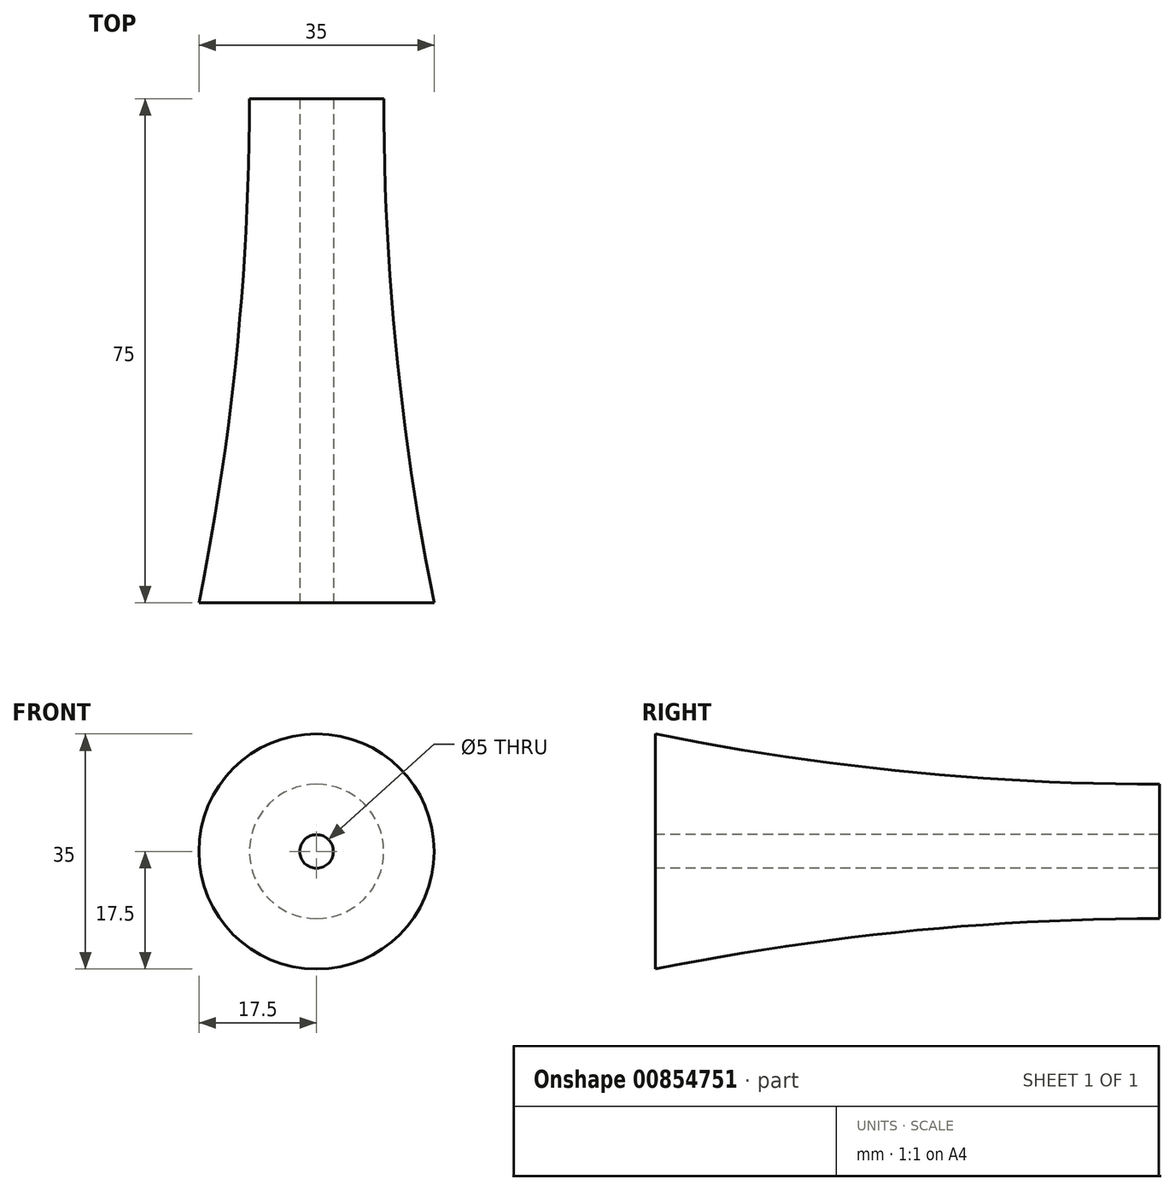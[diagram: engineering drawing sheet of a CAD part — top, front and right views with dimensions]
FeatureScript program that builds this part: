
annotation { "Feature Type Name" : "Feature", "Feature Type Description" : "" }
export const myFeature = defineFeature(function(context is Context, id is Id, definition is map)
    precondition{}
    {
        {
            var Q0;
            Q0=qCreatedBy(makeId("Front.planeOp"),FACE);
            cPlane(context, id + "F0", {"entities" : qUnion([Q0]), "cplaneType" : CPlaneType.OFFSET, "offset" : 75 * mm, "width" : 150 * mm, "height" : 150 * mm});
        }
        {
            var Q0;
            Q0=qCreatedBy(makeId("Front.planeOp"),FACE);
            cPlane(context, id + "F1", {"entities" : qUnion([Q0]), "cplaneType" : CPlaneType.OFFSET, "offset" : 75 * mm, "oppositeDirection" : true, "width" : 150 * mm, "height" : 150 * mm});
        }
        {
            var Q0;
            Q0=qCreatedBy(id+"F0.planeOp",FACE);
            var sketch = newSketch(context, id + "F2", { "sketchPlane" : qUnion([Q0])});
            skCircle(sketch, "E0", {"center": v(0, 0) * mm, "radius": 17.5 * mm});
            skCircle(sketch, "E1", {"center": v(0, 0) * mm, "radius": 2.5 * mm});
            skSolve(sketch);
        }
        {
            var Q0;
            Q0=qCreatedBy(makeId("Front.planeOp"),FACE);
            var sketch = newSketch(context, id + "F3", { "sketchPlane" : qUnion([Q0])});
            skCircle(sketch, "E2", {"center": v(0, 0) * mm, "radius": 10 * mm});
            skSolve(sketch);
        }
        {
            var Q0;
            Q0=qCreatedBy(id+"F1.planeOp",FACE);
            var sketch = newSketch(context, id + "F4", { "sketchPlane" : qUnion([Q0])});
            skCircle(sketch, "E3", {"center": v(0, 0) * mm, "radius": 17.5 * mm});
            skSolve(sketch);
        }
        {
            var Q0;
            Q0=qCreatedBy(makeId("Right.planeOp"),FACE);
            var sketch = newSketch(context, id + "F5", { "sketchPlane" : qUnion([Q0])});
            skLineSegment(sketch, "E4.0", {"start": v(-75, -17.5) * mm, "end": v(-75, 17.5) * mm});
            skLineSegment(sketch, "E4.1", {"start": v(0, -10) * mm, "end": v(0, 10) * mm});
            skLineSegment(sketch, "E4.2", {"start": v(75, -17.5) * mm, "end": v(75, 17.5) * mm});
            skArc(sketch, "E5", {"start": v(-75, 17.5) * mm, "mid": v(0, 10) * mm, "end": v(75, 17.5) * mm});
            skLineSegment(sketch, "E6", {"start": v(-75, 0) * mm, "end": v(75, 0) * mm});
            skSolve(sketch);
        }
        {
            var Q0;
            {var subQ0=sQuery(id+"F5.wireOp",EDGE,"E5");var subQ1=sQuery(id+"F5.wireOp",EDGE,"E4.0");var subQ2=makeQuery(id+"F5.imprint","INTERSECT",VERTEX,{"derivedFrom":[subQ1,subQ0]});Q0=makeQuery(id+"F5.imprint","IMPRINT",FACE,{"disambiguationData":[TD([[makeQuery(id+"F5.imprint","IMPRINT",EDGE,{"disambiguationData":[TD([[subQ2,1.0]])],"derivedFrom":subQ1}),-1.0]])]});}
            var Q1;
            {var subQ0=sQuery(id+"F5.wireOp",EDGE,"E5");var subQ1=sQuery(id+"F5.wireOp",EDGE,"E4.1");var subQ2=makeQuery(id+"F5.imprint","INTERSECT",VERTEX,{"derivedFrom":[subQ1,subQ0]});Q1=makeQuery(id+"F5.imprint","IMPRINT",FACE,{"disambiguationData":[TD([[makeQuery(id+"F5.imprint","IMPRINT",EDGE,{"disambiguationData":[TD([[subQ2,1.0]])],"derivedFrom":subQ1}),-1.0]])]});}
            var Q2;
            Q2=sQuery(id+"F5.wireOp",EDGE,"E6");
            revolve(context, id + "F6", {"surfaceOperationType" : NewSurfaceOperationType.NEW, "entities" : qUnion([Q0, Q1]), "axis" : qUnion([Q2]), "revolveType" : RevolveType.FULL});
        }
        {
            var Q0;
            Q0=makeQuery(id+"F2.imprint","IMPRINT",FACE,{"disambiguationData":[TD([[makeQuery(id+"F2.imprint","IMPRINT",EDGE,{"derivedFrom":sQuery(id+"F2.wireOp",EDGE,"E1")}),1.0]])]});
            extrude(context, id + "F7", {"entities" : qUnion([Q0]), "operationType" : NewBodyOperationType.REMOVE, "endBound" : BoundingType.THROUGH_ALL, "oppositeDirection" : true, "depth" : 25 * mm, "offsetDistance" : 25 * mm});
        }
        {
            var Q0;
            Q0=qCreatedBy(makeId("Front.planeOp"),FACE);
            var sketch = newSketch(context, id + "F8", { "sketchPlane" : qUnion([Q0])});
            skCircle(sketch, "E7", {"center": v(0, 0) * mm, "radius": 25 * mm});
            skSolve(sketch);
        }
        {
            var Q0;
            Q0 = qSketchRegion(id + "F8", true);
            extrude(context, id + "F9", {"entities" : qUnion([Q0]), "operationType" : NewBodyOperationType.REMOVE, "endBound" : BoundingType.THROUGH_ALL, "oppositeDirection" : true, "depth" : 25 * mm, "offsetDistance" : 25 * mm});
        }
    });
